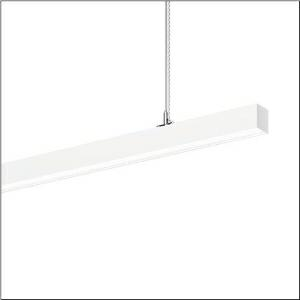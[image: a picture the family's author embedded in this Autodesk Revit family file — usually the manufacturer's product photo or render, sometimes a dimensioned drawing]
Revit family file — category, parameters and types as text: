
# Revit family: silica_r__21_51mx33db49wb_5808
name_source: partatom
category: Lighting Fixtures
units: mm (PartAtom-declared; Revit-internal decimal feet)

## family parameters
Cut with Voids When Loaded = No
Host = Face
Light Source = No
Part Type = Normal
Room Calculation Point = No
Round Connector Dimension = Use Diameter
Shared = No

## types (1)
- --- (1 x LED, 7390 lm, 48.3 W, 4000K)
    Apparent Load = 48 VA
    CIE Flux Codes = 78 96 99 55 100
    Color Rendering = 80
    Color Temperature = 4000K
    Default Elevation = 1800 mm
    Description = Silica® 21, office luminaire, primary optical cover: prismatic diffuser, of PMMA, CAT 2 (L<= 3000cd/m²), light emission: direct/indirect distribution, primary light characteristic: symmetric, installation type: suspended mounting, LED, rated luminous flux: 7.390lm, luminous efficacy: 153lm/W, light colour: 840, colour temperature: 4000K, control gear: DALI 2, with terminal, 3+2-pole, max. 2.5mm², mains connection: 220..240V, AC, 50/60Hz, rated input power: 48.3W, luminaire housing, of aluminium, traffic white (RAL 9016), length: 1.504mm, width: 53mm, height: 53mm, protection rating (complete): IP20, insulation class (complete): insulation class I (protective earthing), certification: CE, permissible operating ambient temperature: 0..+35°C, standard: EN 50419, packaging unit: 1 piece
    Height = 53 mm
    Lamp = 1 x LED
    Lamp Light Flux = 7390 lm
    Lamp Power = 48.3 W
    Lamp count = 1
    Length = 1504 mm
    Luminous efficacy = 153 lm/W
    Manufacturer = Siteco
    ModVariant = No
    Model = 51MX33DB49WB
    Mounting Place = Ceiling
    Mounting Type = Pendant
    Number of Poles = 1
    OnlyDefault = Yes
    Power Factor = 1
    Product Name = Silica® 21
    Product group = office luminaire | ceiling pendant
    ProductGroupID = 904
    Protection Class = Protection class I
    Protection Degree = IP 20
    RLX_Detail_Level = 1
    RLX_Emergency_Light_Flux = 0 lm
    RLX_Emergency_Type = 0
    RLX_Emergency_Type_DB = No
    RlxData = <blob elided: 21389 chars, md5=530ea061>
    Socket = socket
    Standby Power = 0 W
    System Light Flux = 7390 lm
    System Power = 48 W
    Type Comments = factory setting: luminous flux: 100 % | dim-lin: 254 | 323 mA
    Type Image = l_1349007.jpg
    URL = http://relux.com
    VarID = @adj_118210
    Voltage = 0 V
    Weight = 0.00 kg
    Width = 53 mm

## geometry (parser evidence)
native form markers: Blend x4, Sweep x13
no freeform markers — native parametric forms only
